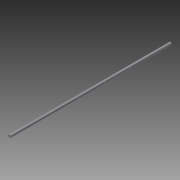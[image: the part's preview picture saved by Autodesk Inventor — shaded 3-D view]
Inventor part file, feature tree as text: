
AUTODESK INVENTOR PART (.ipt)
format: ipt  version: 2013 (Build 170138000, 138)  size: 100,352 bytes
history: native  units: in
note: dims shown in document units (in); Inventor stores cm internally (conversion verified against a paired STEP export)
features: sketch x2, extrude x1, plane x1, hole x1
ambient origin geometry x8: Origin, YZ Plane, XZ Plane, XY Plane, X Axis, Y Axis, Z Axis, Center Point
bodies: Solid1 (feature_tree)
feature tree (5):
  extrude  "Extrusion1"  Depth=0.091in
  plane  "Work Plane1"
  hole  "Hole1"  [1 undecoded]
  sketch  "Sketch1"  dims[d0=0.675in d2=0.091in]
  sketch  "Sketch2"  dims[d3=39.75in d4=0.0in d5=10.13in d6=16.63in d7=23.13in d8=29.63in d9=0.2in d10=0.75in d11=0.375in d12=0.25in d13=0.5635in d14=1.0in d15=0.8108in]
note: 1 required parameter value undecoded (feature->parameter linkage not recoverable at this tier; creation-order binding heuristic only, values carry confidence <= 0.55)
